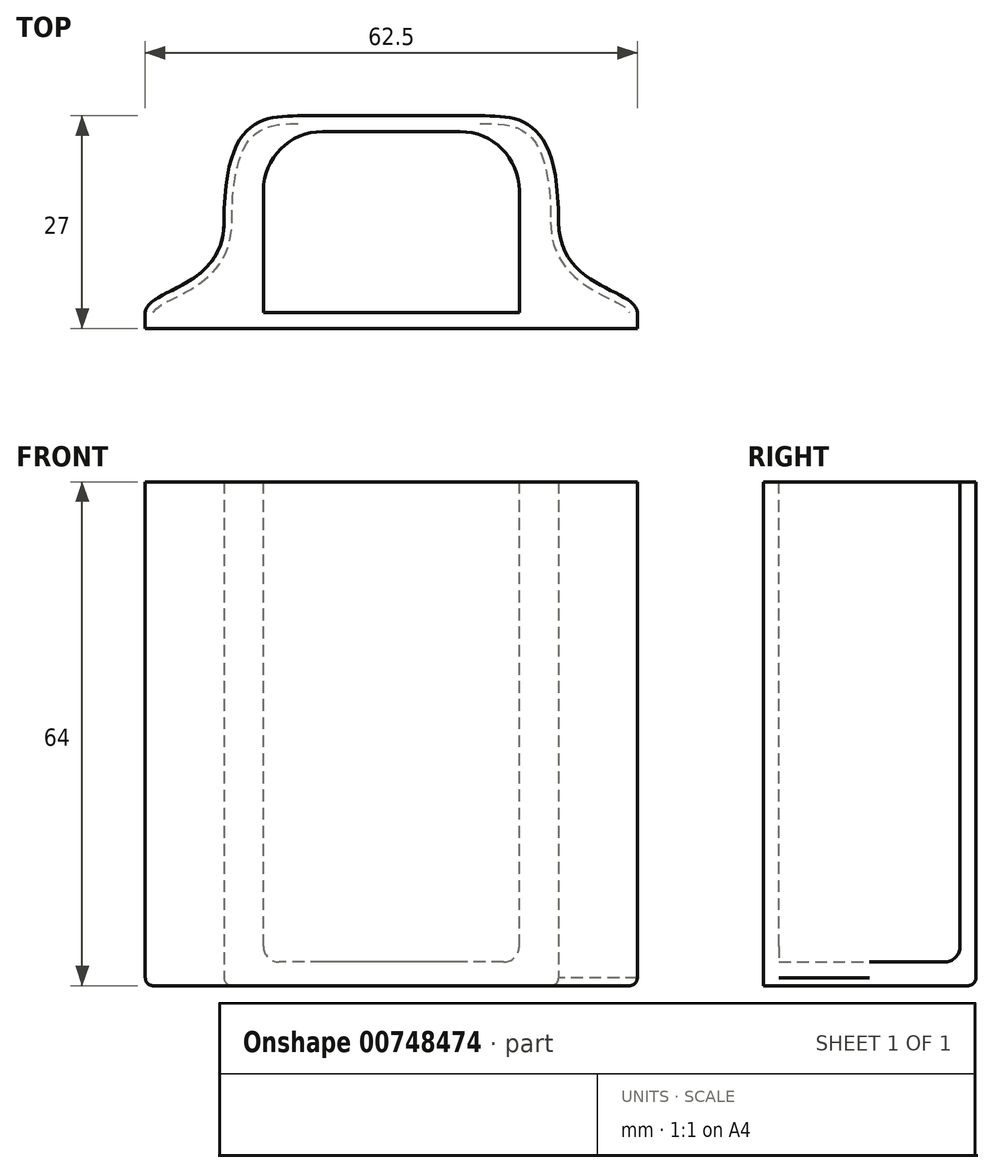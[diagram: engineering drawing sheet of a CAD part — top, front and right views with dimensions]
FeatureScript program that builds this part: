
annotation { "Feature Type Name" : "Feature", "Feature Type Description" : "" }
export const myFeature = defineFeature(function(context is Context, id is Id, definition is map)
    precondition{}
    {
        {
            var Q0;
            Q0=qCreatedBy(makeId("Top.planeOp"),FACE);
            var sketch = newSketch(context, id + "F0", { "sketchPlane" : qUnion([Q0])});
            skLineSegment(sketch, "E0.bottom", {"start": v(16.25, -11.5) * mm, "end": v(-16.25, -11.5) * mm, "construction": true});
            skLineSegment(sketch, "E0.top", {"start": v(16.25, 11.5) * mm, "end": v(-16.25, 11.5) * mm, "construction": true});
            skLineSegment(sketch, "E0.left", {"start": v(16.25, -11.5) * mm, "end": v(16.25, 11.5) * mm, "construction": true});
            skLineSegment(sketch, "E0.right", {"start": v(-16.25, -11.5) * mm, "end": v(-16.25, 11.5) * mm, "construction": true});
            skPoint(sketch, "E0.middle", {"position": v(0, 0) * mm});
            skLineSegment(sketch, "E1.bottom", {"start": v(21.25, -13.5) * mm, "end": v(-21.25, -13.5) * mm});
            skLineSegment(sketch, "E1.top", {"start": v(21.25, 13.5) * mm, "end": v(-11.25, 13.5) * mm});
            skLineSegment(sketch, "E1.left", {"start": v(21.25, -13.5) * mm, "end": v(21.25, -11.41) * mm});
            skLineSegment(sketch, "E2", {"start": v(-21.25, -13.5) * mm, "end": v(-31.25, -13.5) * mm});
            skLineSegment(sketch, "E3", {"start": v(-31.25, -13.5) * mm, "end": v(-31.25, -11.52) * mm});
            skFitSpline(sketch, "E4", {"points": [v(-21.25, 0) * mm, v(-31.25, -11.52) * mm], "startDerivative": vector(0, -25.5) * mm, "endDerivative": vector(0, -9.06) * mm});
            skLineSegment(sketch, "E5", {"start": v(-31.25, -13.5) * mm, "end": v(-31.25, 0) * mm, "construction": true});
            skFitSpline(sketch, "E6", {"points": [v(-21.25, 0) * mm, v(-11.25, 13.5) * mm], "startDerivative": vector(0, 40.5) * mm, "endDerivative": vector(15, 0) * mm});
            skFitSpline(sketch, "E7.0", {"points": [v(-19.25, 0) * mm, v(-19.25, -1.14) * mm, v(-19.56, -3.24) * mm, v(-20.8, -5.8) * mm, v(-22.54, -7.73) * mm, v(-24.14, -8.9) * mm, v(-25.4, -9.64) * mm, v(-26.3, -10.12) * mm, v(-27.14, -10.55) * mm, v(-27.77, -10.87) * mm, v(-28.22, -11.1) * mm, v(-28.52, -11.27) * mm, v(-28.78, -11.43) * mm, v(-29, -11.57) * mm, v(-29.17, -11.7) * mm, v(-29.26, -11.77) * mm, v(-29.3, -11.81) * mm, v(-29.32, -11.83) * mm, v(-29.33, -11.84) * mm, v(-29.34, -11.85) * mm, v(-29.34, -11.85) * mm, v(-29.34, -11.85) * mm, v(-29.34, -11.85) * mm, v(-29.34, -11.85) * mm, v(-29.34, -11.85) * mm, v(-29.35, -11.86) * mm, v(-29.36, -11.87) * mm, v(-29.37, -11.9) * mm, v(-29.38, -11.91) * mm, v(-29.4, -11.92) * mm]});
            skLineSegment(sketch, "E8", {"start": v(-18.17, 8.15) * mm, "end": v(-18.17, -11.41) * mm});
            skLineSegment(sketch, "E9", {"start": v(-18.17, -11.41) * mm, "end": v(-26.83, -11.41) * mm});
            skLineSegment(sketch, "E10", {"start": v(-26.83, -11.41) * mm, "end": v(-26.83, -10.4) * mm});
            skFitSpline(sketch, "E11.0", {"points": [v(-19.25, 0) * mm, v(-19.25, 1.63) * mm, v(-19.1, 4.43) * mm, v(-18.5, 7.43) * mm, v(-17.82, 9.03) * mm, v(-17.24, 9.88) * mm, v(-16.8, 10.35) * mm, v(-16.32, 10.7) * mm, v(-15.65, 11.06) * mm, v(-14.62, 11.36) * mm, v(-13.07, 11.5) * mm, v(-11.88, 11.5) * mm, v(-11.25, 11.5) * mm]});
            skFitSpline(sketch, "E12.MirrorCS", {"points": [v(21.25, 0) * mm, v(11.25, 13.5) * mm], "startDerivative": vector(0, 40.5) * mm, "endDerivative": vector(-15, 0) * mm});
            skLineSegment(sketch, "E13.MirrorCS", {"start": v(18.17, 8.15) * mm, "end": v(18.17, -11.41) * mm});
            skLineSegment(sketch, "E14.MirrorCS", {"start": v(18.17, -11.41) * mm, "end": v(26.83, -11.41) * mm});
            skLineSegment(sketch, "E15.MirrorCS", {"start": v(26.83, -11.41) * mm, "end": v(26.83, -10.4) * mm});
            skFitSpline(sketch, "E16.MirrorCS", {"points": [v(21.25, 0) * mm, v(31.25, -11.52) * mm], "startDerivative": vector(0, -25.5) * mm, "endDerivative": vector(0, -9.06) * mm});
            skLineSegment(sketch, "E17.MirrorCS", {"start": v(31.25, -13.5) * mm, "end": v(31.25, -11.52) * mm});
            skLineSegment(sketch, "E18.MirrorCS", {"start": v(21.25, -13.5) * mm, "end": v(31.25, -13.5) * mm});
            skFitSpline(sketch, "E19.0", {"points": [v(19.25, 0) * mm, v(19.25, 1.63) * mm, v(19.1, 4.43) * mm, v(18.5, 7.43) * mm, v(17.82, 9.03) * mm, v(17.24, 9.88) * mm, v(16.8, 10.35) * mm, v(16.32, 10.7) * mm, v(15.65, 11.06) * mm, v(14.62, 11.36) * mm, v(13.07, 11.5) * mm, v(11.88, 11.5) * mm, v(11.25, 11.5) * mm]});
            skFitSpline(sketch, "E20.0", {"points": [v(19.25, 0) * mm, v(19.25, -1.14) * mm, v(19.56, -3.24) * mm, v(20.8, -5.8) * mm, v(22.54, -7.73) * mm, v(24.14, -8.9) * mm, v(25.4, -9.64) * mm, v(26.3, -10.12) * mm, v(27.14, -10.55) * mm, v(27.77, -10.87) * mm, v(28.22, -11.1) * mm, v(28.52, -11.27) * mm, v(28.78, -11.43) * mm, v(29, -11.57) * mm, v(29.17, -11.7) * mm, v(29.26, -11.77) * mm, v(29.3, -11.81) * mm, v(29.32, -11.83) * mm, v(29.33, -11.84) * mm, v(29.34, -11.85) * mm, v(29.34, -11.85) * mm, v(29.34, -11.85) * mm, v(29.34, -11.85) * mm, v(29.34, -11.85) * mm, v(29.34, -11.85) * mm, v(29.35, -11.86) * mm, v(29.36, -11.87) * mm, v(29.37, -11.9) * mm, v(29.38, -11.91) * mm, v(29.4, -11.92) * mm]});
            skLineSegment(sketch, "E21.trimOffspring", {"start": v(21.25, 0) * mm, "end": v(21.25, 13.5) * mm});
            skSolve(sketch);
        }
        {
            var Q0;
            Q0=makeQuery(id+"F0.imprint","IMPRINT",FACE,{"disambiguationData":[TD([[makeQuery(id+"F0.imprint","IMPRINT",EDGE,{"derivedFrom":sQuery(id+"F0.wireOp",EDGE,"E1.bottom")}),-1.0]])]});
            extrude(context, id + "F1", {"entities" : qUnion([Q0]), "endBound" : BoundingType.SYMMETRIC, "depth" : 64 * mm, "offsetDistance" : 25 * mm, "hasSecondDirection" : true, "secondDirectionOppositeDirection" : true, "secondDirectionDepth" : 64 * mm});
        }
        {
            var Q0;
            Q0=makeQuery(id+"F1.opExtrude","CAP_FACE",FACE,{"disambiguationData":[OSD([sQuery(id+"F0.wireOp",EDGE,"E1.bottom"),sQuery(id+"F0.wireOp",EDGE,"E1.top"),sQuery(id+"F0.wireOp",EDGE,"E1.left"),sQuery(id+"F0.wireOp",EDGE,"E1.right")])],"isStart":false});
            var sketch = newSketch(context, id + "F2", { "sketchPlane" : qUnion([Q0])});
            skLineSegment(sketch, "E22.0", {"start": v(-16.25, -11.5) * mm, "end": v(-16.25, 11.5) * mm});
            skLineSegment(sketch, "E22.1", {"start": v(16.25, 11.5) * mm, "end": v(-16.25, 11.5) * mm});
            skLineSegment(sketch, "E22.2", {"start": v(16.25, -11.5) * mm, "end": v(16.25, 11.5) * mm});
            skLineSegment(sketch, "E22.3", {"start": v(16.25, -11.5) * mm, "end": v(-16.25, -11.5) * mm});
            skSolve(sketch);
        }
        {
            var Q0;
            Q0 = qSketchRegion(id + "F2", true);
            extrude(context, id + "F3", {"entities" : qUnion([Q0]), "operationType" : NewBodyOperationType.REMOVE, "oppositeDirection" : true, "depth" : 61 * mm, "offsetDistance" : 25 * mm});
        }
        {
            var Q0;
            Q0=makeQuery(id+"F3.boolean.opBoolean","COPY",EDGE,{"derivedFrom":makeQuery(id+"F3.opExtrude","SWEPT_EDGE",EDGE,{"disambiguationData":[OSD([sQuery(id+"F2.wireOp",EDGE,"E22.0"),sQuery(id+"F2.wireOp",EDGE,"E22.1")])]})});
            var Q1;
            Q1=makeQuery(id+"F3.boolean.opBoolean","COPY",EDGE,{"derivedFrom":makeQuery(id+"F3.opExtrude","SWEPT_EDGE",EDGE,{"disambiguationData":[OSD([sQuery(id+"F2.wireOp",EDGE,"E22.1"),sQuery(id+"F2.wireOp",EDGE,"E22.2")])]})});
            fillet(context, id + "F4", {"entities" : qUnion([Q0, Q1]), "radius" : 7.5 * mm, "tangentPropagation" : true, "allowEdgeOverflow" : false});
        }
        {
            var Q0;
            Q0=makeQuery(id+"F3.boolean.opBoolean","COPY",EDGE,{"derivedFrom":makeQuery(id+"F3.opExtrude","CAP_EDGE",EDGE,{"disambiguationData":[OSD([sQuery(id+"F2.wireOp",EDGE,"E22.1")])],"isStart":false})});
            fillet(context, id + "F5", {"entities" : qUnion([Q0]), "radius" : 2 * mm, "tangentPropagation" : true, "allowEdgeOverflow" : false});
        }
        {
            var Q0;
            Q0=makeQuery(id+"F1.opExtrude","CAP_EDGE",EDGE,{"disambiguationData":[OSD([sQuery(id+"F0.wireOp",EDGE,"E1.top")])],"isStart":true});
            fillet(context, id + "F6", {"entities" : qUnion([Q0]), "radius" : 1 * mm, "tangentPropagation" : true, "allowEdgeOverflow" : false});
        }
    });
